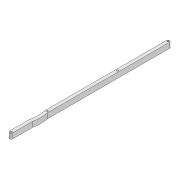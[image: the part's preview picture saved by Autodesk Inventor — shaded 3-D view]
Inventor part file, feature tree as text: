
AUTODESK INVENTOR PART (.ipt)
format: ipt  version: 2022 (Build 260153000, 153)  size: 102,912 bytes
history: native  units: mm
features: extrude x1, other x1, sketch x1
ambient origin geometry x8: Origin, YZ Plane, XZ Plane, XY Plane, X Axis, Y Axis, Z Axis, Center Point
bodies: Solid1 (feature_tree)
feature tree (3):
  extrude  "Extrusion1"  Depth=296.686mm
  other  "Work Axis1"
  sketch  "Sketch1"  dims[d0=6.0mm d1=296.686mm d2=3.0mm d3=3.0mm d4=10.0mm d5=0.0mm d6=3.0mm d7=200.914mm d8=3.0mm d9=68.172mm d10=60.0mm d11=3.0mm d12=30.0mm d13=60.0mm]
